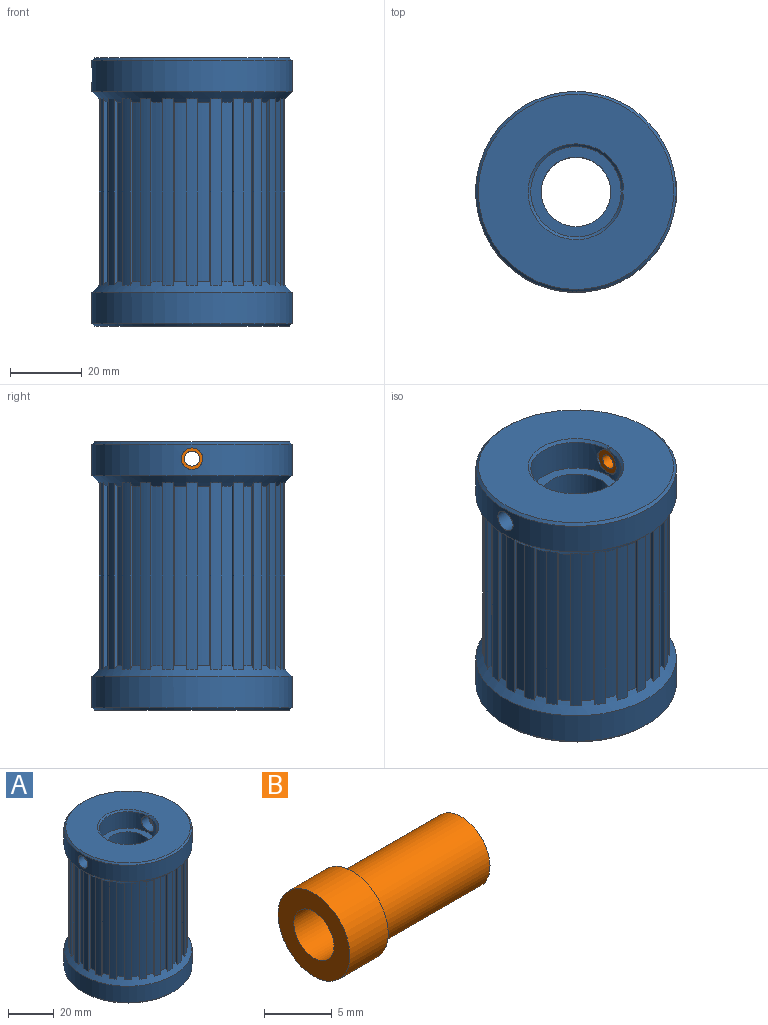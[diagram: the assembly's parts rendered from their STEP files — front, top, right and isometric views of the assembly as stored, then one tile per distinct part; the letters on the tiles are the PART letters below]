
ASSEMBLY  parts=2 mates=1
PART A: 119 faces, bbox 56x56x75 mm
  f0: cylinder r=3mm len=11.38mm, axis (1,0,0), area 212.9mm2, adj f107,f114
  f1: plane 1x0.1mm, normal (-0.61,-0.79,0), area 0.1mm2, adj f2,f101,f104,f112
  f2: plane 1x0.1mm, normal (-0.61,0.79,0), area 0.1mm2, adj f1,f101,f104,f112
  f3: cylinder r=25mm len=50mm, axis (0,0,-1), area 176.2mm2, adj f4,f98,f106,f108
  f4: plane 52x0.95mm, normal (-0.32,-0.95,0), area 51mm2, adj f3,f5,f106,f108
  f5: cylinder r=26mm len=52mm, axis (0,0,-1), area 163.4mm2, adj f4,f6,f106,f108
  f6: plane 52x0.98mm, normal (0.2,0.98,0), area 51mm2, adj f5,f7,f106,f108
  f7: cylinder r=25mm len=50mm, axis (0,0,-1), area 176.2mm2, adj f6,f8,f106,f108
  f8: plane 52x1mm, normal (-0.06,-1,0), area 51mm2, adj f7,f9,f106,f108
  f9: cylinder r=26mm len=52mm, axis (0,0,-1), area 163.4mm2, adj f8,f10,f106,f108
  f10: plane 52x1mm, normal (-0.06,1,0), area 51mm2, adj f9,f11,f106,f108
  f11: cylinder r=25mm len=50mm, axis (0,0,-1), area 176.2mm2, adj f10,f12,f106,f108
  f12: plane 52x0.98mm, normal (0.2,-0.98,0), area 51mm2, adj f11,f13,f106,f108
  f13: cylinder r=26mm len=52mm, axis (0,0,-1), area 163.4mm2, adj f12,f14,f106,f108
  f14: plane 52x0.95mm, normal (-0.32,0.95,0), area 51mm2, adj f13,f15,f106,f108
  f15: cylinder r=25mm len=50mm, axis (0,0,-1), area 176.2mm2, adj f14,f16,f106,f108
  f16: plane 52x0.89mm, normal (0.45,-0.89,0), area 51mm2, adj f15,f17,f106,f108
  f17: cylinder r=26mm len=52mm, axis (0,0,-1), area 163.4mm2, adj f16,f18,f106,f108
  f18: plane 52x0.83mm, normal (-0.55,0.83,0), area 51mm2, adj f17,f19,f106,f108
  f19: cylinder r=25mm len=50mm, axis (0,0,-1), area 176.2mm2, adj f18,f20,f106,f108
  f20: plane 52x0.75mm, normal (0.66,-0.75,0), area 51mm2, adj f19,f21,f106,f108
  f21: cylinder r=26mm len=52mm, axis (0,0,-1), area 163.4mm2, adj f20,f22,f106,f108
  f22: plane 52x0.75mm, normal (-0.75,0.66,0), area 51mm2, adj f21,f23,f106,f108
  f23: cylinder r=25mm len=50mm, axis (0,0,-1), area 176.2mm2, adj f22,f24,f106,f108
  f24: plane 52x0.83mm, normal (0.83,-0.55,0), area 51mm2, adj f23,f25,f106,f108
  f25: cylinder r=26mm len=52mm, axis (0,0,-1), area 163.4mm2, adj f24,f26,f106,f108
  f26: plane 52x0.89mm, normal (-0.89,0.45,0), area 51mm2, adj f25,f27,f106,f108
  f27: cylinder r=25mm len=50mm, axis (0,0,-1), area 176.2mm2, adj f26,f28,f106,f108
  f28: plane 52x0.95mm, normal (0.95,-0.32,0), area 51mm2, adj f27,f29,f106,f108
  f29: cylinder r=26mm len=52mm, axis (0,0,-1), area 163.4mm2, adj f28,f30,f106,f108
  f30: plane 52x0.98mm, normal (-0.98,0.2,0), area 51mm2, adj f29,f31,f106,f108
  f31: cylinder r=25mm len=50mm, axis (0,0,-1), area 176.2mm2, adj f30,f32,f106,f108
  f32: plane 52x1mm, normal (1,-0.06,0), area 51mm2, adj f31,f33,f106,f108
  f33: cylinder r=26mm len=52mm, axis (0,0,-1), area 163.4mm2, adj f32,f34,f106,f108
  f34: plane 52x1mm, normal (-1,-0.06,0), area 51mm2, adj f33,f35,f106,f108
  f35: cylinder r=25mm len=50mm, axis (0,0,-1), area 176.2mm2, adj f34,f36,f106,f108
  f36: plane 52x0.98mm, normal (0.98,0.2,0), area 51mm2, adj f35,f37,f106,f108
  f37: cylinder r=26mm len=52mm, axis (0,0,-1), area 163.4mm2, adj f36,f38,f106,f108
  f38: plane 52x0.95mm, normal (-0.95,-0.32,0), area 51mm2, adj f37,f39,f106,f108
  f39: cylinder r=25mm len=50mm, axis (0,0,-1), area 176.2mm2, adj f38,f40,f106,f108
  f40: plane 52x0.89mm, normal (0.89,0.45,0), area 51mm2, adj f39,f41,f106,f108
  f41: cylinder r=26mm len=52mm, axis (0,0,-1), area 163.4mm2, adj f40,f42,f106,f108
  f42: plane 52x0.83mm, normal (-0.83,-0.55,0), area 51mm2, adj f41,f43,f106,f108
  f43: cylinder r=25mm len=50mm, axis (0,0,-1), area 176.2mm2, adj f42,f44,f106,f108
  f44: plane 52x0.75mm, normal (0.75,0.66,0), area 51mm2, adj f43,f45,f106,f108
  f45: cylinder r=26mm len=52mm, axis (0,0,-1), area 163.4mm2, adj f44,f46,f106,f108
  f46: plane 52x0.75mm, normal (-0.66,-0.75,0), area 51mm2, adj f45,f47,f106,f108
  f47: cylinder r=25mm len=50mm, axis (0,0,-1), area 176.2mm2, adj f46,f48,f106,f108
  f48: plane 52x0.83mm, normal (0.55,0.83,0), area 51mm2, adj f47,f49,f106,f108
  f49: cylinder r=26mm len=52mm, axis (0,0,-1), area 163.4mm2, adj f48,f50,f106,f108
  f50: plane 52x0.89mm, normal (-0.45,-0.89,0), area 51mm2, adj f49,f51,f106,f108
  f51: cylinder r=25mm len=50mm, axis (0,0,-1), area 176.2mm2, adj f50,f52,f106,f108
  f52: plane 52x0.95mm, normal (0.32,0.95,0), area 51mm2, adj f51,f53,f106,f108
  f53: cylinder r=26mm len=52mm, axis (0,0,-1), area 163.4mm2, adj f52,f54,f106,f108
  f54: plane 52x0.98mm, normal (-0.2,-0.98,0), area 51mm2, adj f53,f55,f106,f108
  f55: cylinder r=25mm len=50mm, axis (0,0,-1), area 176.2mm2, adj f54,f56,f106,f108
  f56: plane 52x1mm, normal (0.06,1,0), area 51mm2, adj f55,f57,f106,f108
  f57: cylinder r=26mm len=52mm, axis (0,0,-1), area 163.4mm2, adj f56,f58,f106,f108
  f58: plane 52x1mm, normal (0.06,-1,0), area 51mm2, adj f57,f59,f106,f108
  f59: cylinder r=25mm len=50mm, axis (0,0,-1), area 176.2mm2, adj f58,f60,f106,f108
  f60: plane 52x0.98mm, normal (-0.2,0.98,0), area 51mm2, adj f59,f61,f106,f108
  f61: cylinder r=26mm len=52mm, axis (0,0,-1), area 163.4mm2, adj f60,f62,f106,f108
  f62: plane 52x0.95mm, normal (0.32,-0.95,0), area 51mm2, adj f61,f63,f106,f108
  f63: cylinder r=25mm len=50mm, axis (0,0,-1), area 176.2mm2, adj f62,f64,f106,f108
  f64: plane 52x0.89mm, normal (-0.45,0.89,0), area 51mm2, adj f63,f65,f106,f108
  f65: cylinder r=26mm len=52mm, axis (0,0,-1), area 163.4mm2, adj f64,f66,f106,f108
  f66: plane 52x0.83mm, normal (0.55,-0.83,0), area 51mm2, adj f65,f67,f106,f108
  f67: cylinder r=25mm len=50mm, axis (0,0,-1), area 176.2mm2, adj f66,f68,f106,f108
  f68: plane 52x0.75mm, normal (-0.66,0.75,0), area 51mm2, adj f67,f69,f106,f108
  f69: cylinder r=26mm len=52mm, axis (0,0,-1), area 163.4mm2, adj f68,f70,f106,f108
  f70: plane 52x0.75mm, normal (0.75,-0.66,0), area 51mm2, adj f69,f71,f106,f108
  f71: cylinder r=25mm len=50mm, axis (0,0,-1), area 176.2mm2, adj f70,f72,f106,f108
  f72: plane 52x0.83mm, normal (-0.83,0.55,0), area 51mm2, adj f71,f73,f106,f108
  f73: cylinder r=26mm len=52mm, axis (0,0,-1), area 163.4mm2, adj f72,f74,f106,f108
  f74: plane 52x0.89mm, normal (0.89,-0.45,0), area 51mm2, adj f73,f75,f106,f108
  f75: cylinder r=25mm len=50mm, axis (0,0,-1), area 176.2mm2, adj f74,f76,f106,f108
  f76: plane 52x0.95mm, normal (-0.95,0.32,0), area 51mm2, adj f75,f77,f106,f108
  f77: cylinder r=26mm len=52mm, axis (0,0,-1), area 163.4mm2, adj f76,f78,f106,f108
  f78: plane 52x0.98mm, normal (0.98,-0.2,0), area 51mm2, adj f77,f79,f106,f108
  f79: cylinder r=25mm len=50mm, axis (0,0,-1), area 176.2mm2, adj f78,f80,f106,f108
  f80: plane 52x1mm, normal (-1,0.06,0), area 51mm2, adj f79,f81,f106,f108
  f81: cylinder r=26mm len=52mm, axis (0,0,-1), area 163.4mm2, adj f80,f82,f106,f108
  f82: plane 52x1mm, normal (1,0.06,0), area 51mm2, adj f81,f83,f106,f108
  f83: cylinder r=25mm len=50mm, axis (0,0,-1), area 176.2mm2, adj f82,f84,f106,f108
  f84: plane 52x0.98mm, normal (-0.98,-0.2,0), area 51mm2, adj f83,f85,f106,f108
  f85: cylinder r=26mm len=52mm, axis (0,0,-1), area 163.4mm2, adj f84,f86,f106,f108
  f86: plane 52x0.95mm, normal (0.95,0.32,0), area 51mm2, adj f85,f87,f106,f108
  f87: cylinder r=25mm len=50mm, axis (0,0,-1), area 176.2mm2, adj f86,f88,f106,f108
  f88: plane 52x0.89mm, normal (-0.89,-0.45,0), area 51mm2, adj f87,f89,f106,f108
  f89: cylinder r=26mm len=52mm, axis (0,0,-1), area 163.4mm2, adj f88,f90,f106,f108
  f90: plane 52x0.83mm, normal (0.83,0.55,0), area 51mm2, adj f89,f91,f106,f108
  f91: cylinder r=25mm len=50mm, axis (0,0,-1), area 176.2mm2, adj f90,f92,f106,f108
  f92: plane 52x0.75mm, normal (-0.75,-0.66,0), area 51mm2, adj f91,f93,f106,f108
  f93: cylinder r=26mm len=52mm, axis (0,0,-1), area 163.4mm2, adj f92,f94,f106,f108
  f94: plane 52x0.75mm, normal (0.66,0.75,0), area 51mm2, adj f93,f95,f106,f108
  f95: cylinder r=25mm len=50mm, axis (0,0,-1), area 176.2mm2, adj f94,f96,f106,f108
  f96: plane 52x0.83mm, normal (-0.55,-0.83,0), area 51mm2, adj f95,f97,f106,f108
  f97: cylinder r=26mm len=52mm, axis (0,0,-1), area 163.4mm2, adj f96,f98,f106,f108
  f98: plane 52x0.89mm, normal (0.45,0.89,0), area 51mm2, adj f3,f97,f106,f108
  f99: plane 54.5x54.5mm, normal (0,0,1), area 1771.4mm2, adj f102,f103,f115,f116
  f100: plane 54.5x54.5mm, normal (0,0,-1), area 1989.8mm2, adj f117,f118
  f101: cylinder r=12.62mm len=25.25mm, axis (0,0,1), area 604.5mm2, adj f1,f2,f102,f103,f104,f112,f113,f116
  f102: plane 1.02x0.85mm, normal (-0.61,-0.79,0), area 0.5mm2, adj f99,f101,f103,f112,f116
  f103: plane 1.02x0.85mm, normal (-0.61,0.79,0), area 0.5mm2, adj f99,f101,f102,f112,f116
  f104: plane 25.25x25.25mm, normal (0,0,1), area 205.1mm2, adj f1,f2,f101,f105
  f105: cylinder r=9.7mm len=64.75mm, axis (0,0,-1), area 3946.3mm2, adj f104,f118
  f106: cone r=25mm half-angle=45deg, axis (0,0,1), area 601.8mm2, adj f3,f4,f5,f6,f7,f8,f9,f10
  f107: cylinder r=28mm len=56mm, axis (0,0,1), area 1482.9mm2, adj f0,f106,f110,f115
  f108: cone r=25mm half-angle=45deg, axis (0,0,-1), area 601.8mm2, adj f3,f4,f5,f6,f7,f8,f9,f10
  f109: cylinder r=28mm len=56mm, axis (0,0,1), area 1539.4mm2, adj f108,f117
  f110: cylinder r=3mm len=11.38mm, axis (1,0,0), area 212.9mm2, adj f107,f111
  f111: plane 7.5x7.5mm, normal (-1,0,0), area 15.9mm2, adj f110,f112
  f112: cylinder r=3.75mm len=7.5mm, axis (1,0,0), area 100.9mm2, adj f1,f2,f101,f102,f103,f111
  f113: cylinder r=3.75mm len=7.5mm, axis (1,0,0), area 100.9mm2, adj f101,f114
  f114: plane 7.5x7.5mm, normal (1,0,0), area 15.9mm2, adj f0,f113
  f115: cone r=27.25mm half-angle=45deg, axis (0,0,-1), area 184.1mm2, adj f99,f107
  f116: cone r=13.38mm half-angle=45deg, axis (0,0,1), area 85.9mm2, adj f99,f101,f102,f103
  f117: cone r=28mm half-angle=45deg, axis (0,0,1), area 184.1mm2, adj f100,f109
  f118: cone r=9.7mm half-angle=45deg, axis (0,0,-1), area 67.1mm2, adj f100,f105
PART B: 6 faces, bbox 15.4x7.5x7.5 mm
  f0: cylinder r=3.75mm len=7.5mm, axis (-1,0,0), area 94.2mm2, adj f1,f2
  f1: plane 7.5x7.5mm, normal (1,0,0), area 15.9mm2, adj f0,f3
  f2: plane 7.5x7.5mm, normal (-1,0,0), area 30.3mm2, adj f0,f5
  f3: cylinder r=3mm len=11.38mm, axis (-1,0,0), area 214.4mm2, adj f1,f4
  f4: plane 6x6mm, normal (1,0,0), area 14.4mm2, adj f3,f5
  f5: cylinder r=2.1mm len=15.38mm, axis (1,0,0), area 202.9mm2, adj f2,f4
PLACE A at identity
PLACE B t=(-37.38,0,0)mm
MATE fastened A.f0 <-> B.f0  axis (1,0,0) through (16.62,0,70.25)mm
